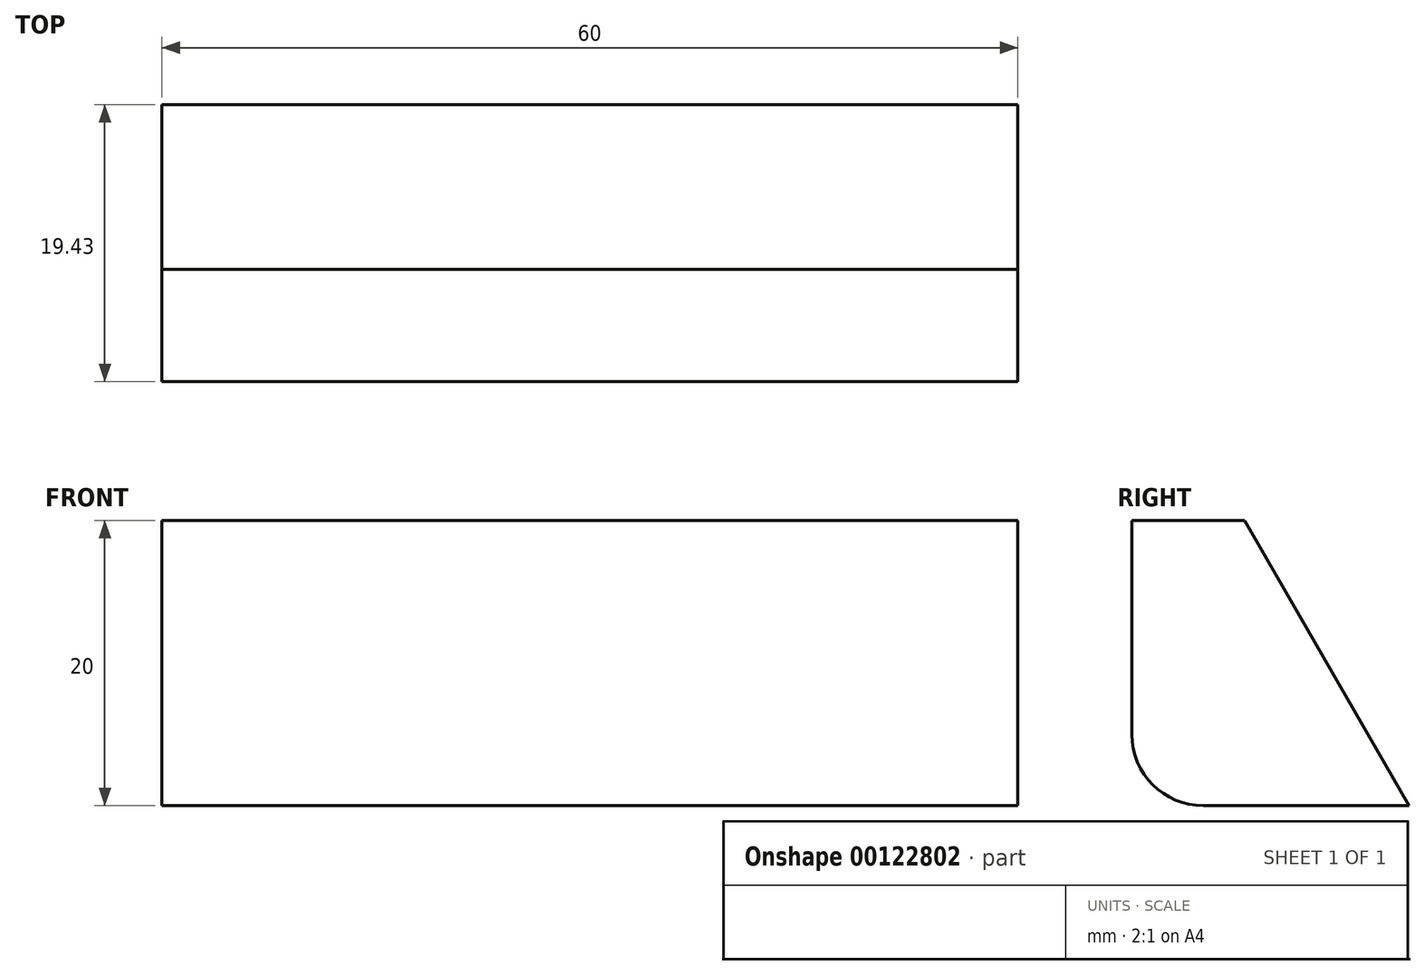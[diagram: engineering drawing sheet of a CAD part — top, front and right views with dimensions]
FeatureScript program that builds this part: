
annotation { "Feature Type Name" : "Feature", "Feature Type Description" : "" }
export const myFeature = defineFeature(function(context is Context, id is Id, definition is map)
    precondition{}
    {
        {
            var Q0;
            Q0=qCreatedBy(makeId("Right.planeOp"),FACE);
            var sketch = newSketch(context, id + "F0", { "sketchPlane" : qUnion([Q0])});
            skLineSegment(sketch, "E0", {"start": v(5.78, -23.29) * mm, "end": v(-24.22, -23.29) * mm});
            skPoint(sketch, "E1", {"position": v(-24.22, -23.29) * mm});
            skLineSegment(sketch, "E2", {"start": v(-24.22, -10.79) * mm, "end": v(-24.22, -35.79) * mm});
            skLineSegment(sketch, "E3", {"start": v(-24.22, -35.79) * mm, "end": v(5.78, -35.79) * mm});
            skLineSegment(sketch, "E4", {"start": v(-24.22, -10.79) * mm, "end": v(-9.79, -35.79) * mm});
            skLineSegment(sketch, "E5", {"start": v(-24.22, -15.79) * mm, "end": v(-21.33, -15.79) * mm});
            skLineSegment(sketch, "E6.bottom", {"start": v(-24.22, -15.79) * mm, "end": v(-29.22, -15.79) * mm});
            skLineSegment(sketch, "E6.top", {"start": v(-24.22, -35.79) * mm, "end": v(-29.22, -35.79) * mm});
            skLineSegment(sketch, "E6.left", {"start": v(-24.22, -15.79) * mm, "end": v(-24.22, -35.79) * mm});
            skLineSegment(sketch, "E6.right", {"start": v(-29.22, -15.79) * mm, "end": v(-29.22, -35.79) * mm});
            skSolve(sketch);
        }
        {
            var Q0;
            {var subQ0=sQuery(id+"F0.wireOp",EDGE,"E6.left");var subQ1=sQuery(id+"F0.wireOp",EDGE,"E0");var subQ2=makeQuery(id+"F0.imprint","INTERSECT",VERTEX,{"derivedFrom":[subQ1,subQ0]});Q0=makeQuery(id+"F0.imprint","IMPRINT",FACE,{"disambiguationData":[TD([[makeQuery(id+"F0.imprint","IMPRINT",EDGE,{"disambiguationData":[TD([[subQ2,1.0]])],"derivedFrom":subQ1}),1.0]])]});}
            var Q1;
            {var subQ5=sQuery(id+"F0.wireOp",EDGE,"E5");Q1=makeQuery(id+"F0.imprint","IMPRINT",FACE,{"disambiguationData":[TD([[makeQuery(id+"F0.imprint","IMPRINT",EDGE,{"derivedFrom":subQ5}),-1.0]])]});}
            var Q2;
            {var subQ3=sQuery(id+"F0.wireOp",EDGE,"E6.bottom");Q2=makeQuery(id+"F0.imprint","IMPRINT",FACE,{"disambiguationData":[TD([[makeQuery(id+"F0.imprint","IMPRINT",EDGE,{"derivedFrom":subQ3}),1.0]])]});}
            extrude(context, id + "F1", {"entities" : qUnion([Q0, Q1, Q2]), "endBound" : BoundingType.SYMMETRIC, "depth" : 60 * mm});
        }
        {
            var Q0;
            Q0=makeQuery(id+"F1.opExtrude","SWEPT_EDGE",EDGE,{"disambiguationData":[OSD([sQuery(id+"F0.wireOp",EDGE,"E6.top"),sQuery(id+"F0.wireOp",EDGE,"E6.right")])]});
            fillet(context, id + "F2", {"entities" : qUnion([Q0]), "radius" : 5 * mm, "tangentPropagation" : true, "allowEdgeOverflow" : false});
        }
    });
